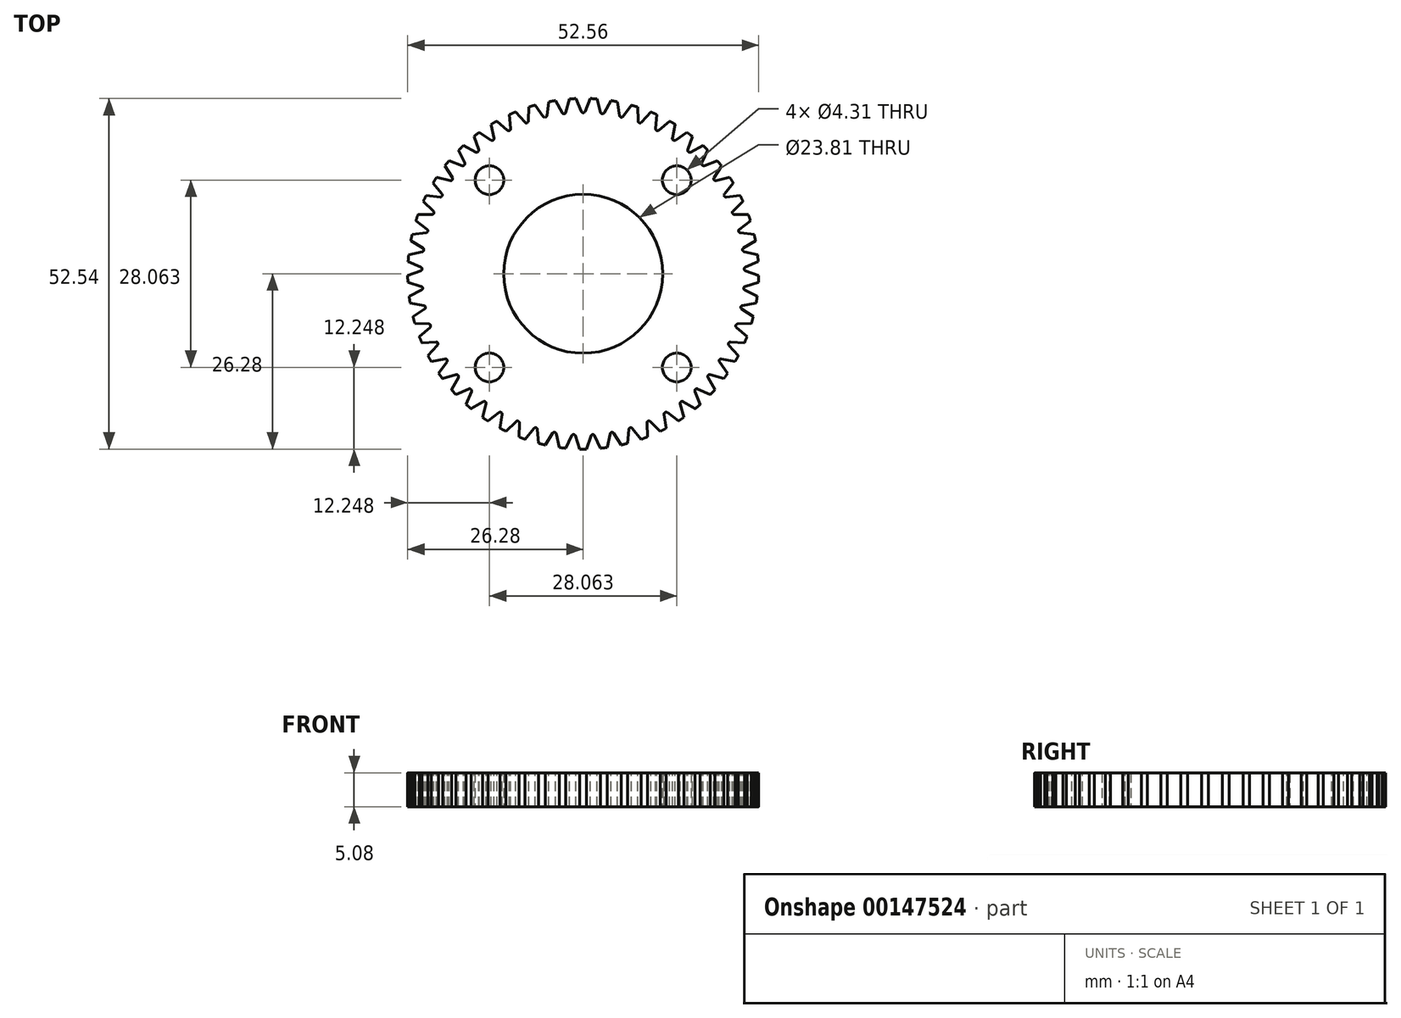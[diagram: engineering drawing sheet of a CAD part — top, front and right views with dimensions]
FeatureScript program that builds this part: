
annotation { "Feature Type Name" : "Feature", "Feature Type Description" : "" }
export const myFeature = defineFeature(function(context is Context, id is Id, definition is map)
    precondition{}
    {
        {
            var Q0;
            Q0=qCreatedBy(makeId("Top.planeOp"),FACE);
            var sketch = newSketch(context, id + "F0", { "sketchPlane" : qUnion([Q0])});
            skCircle(sketch, "E0", {"center": v(0, 0) * mm, "radius": 26.28 * mm});
            skCircle(sketch, "E1", {"center": v(0, 0) * mm, "radius": 11.9 * mm});
            skLineSegment(sketch, "E2.bottom", {"start": v(14.03, -14.03) * mm, "end": v(-14.03, -14.03) * mm, "construction": true});
            skLineSegment(sketch, "E2.top", {"start": v(14.03, 14.03) * mm, "end": v(-14.03, 14.03) * mm, "construction": true});
            skLineSegment(sketch, "E2.left", {"start": v(14.03, -14.03) * mm, "end": v(14.03, 14.03) * mm, "construction": true});
            skLineSegment(sketch, "E2.right", {"start": v(-14.03, -14.03) * mm, "end": v(-14.03, 14.03) * mm, "construction": true});
            skCircle(sketch, "E3", {"center": v(14.03, -14.03) * mm, "radius": 3.97 * mm, "construction": true});
            skCircle(sketch, "E4", {"center": v(14.03, 14.03) * mm, "radius": 2.15 * mm});
            skCircle(sketch, "E5", {"center": v(-14.03, -14.03) * mm, "radius": 2.15 * mm});
            skCircle(sketch, "E6", {"center": v(14.03, -14.03) * mm, "radius": 2.15 * mm});
            skCircle(sketch, "E7", {"center": v(-14.03, 14.03) * mm, "radius": 2.15 * mm});
            skCircle(sketch, "E8", {"center": v(0, 0) * mm, "radius": 15.88 * mm, "construction": true});
            skSolve(sketch);
        }
        {
            var Q0;
            Q0=qSketchRegion(id+"F0",true);
            extrude(context, id + "F1", {"entities" : qUnion([Q0]), "depth" : 5.08 * mm});
        }
        {
            var Q0;
            Q0=makeQuery(id+"F1.opExtrude","CAP_FACE",FACE,{"disambiguationData":[OSD([sQuery(id+"F0.wireOp",EDGE,"E0")])],"isStart":false});
            var sketch = newSketch(context, id + "F2", { "sketchPlane" : qUnion([Q0])});
            skLineSegment(sketch, "E9", {"start": v(0, 0) * mm, "end": v(0, 26.28) * mm});
            skArc(sketch, "E10", {"start": v(1.06, 26.26) * mm, "mid": v(0, 26.28) * mm, "end": v(-1.06, 26.26) * mm});
            skLineSegment(sketch, "E11", {"start": v(-1.06, 26.26) * mm, "end": v(-0.28, 24.32) * mm});
            skLineSegment(sketch, "E12", {"start": v(1.06, 26.26) * mm, "end": v(0.28, 24.32) * mm});
            skArc(sketch, "E13", {"start": v(-0.28, 24.32) * mm, "mid": v(0, 24.13) * mm, "end": v(0.28, 24.32) * mm});
            skLineSegment(sketch, "E14", {"start": v(0, 0) * mm, "end": v(0.7, 26.27) * mm, "construction": true});
            skPoint(sketch, "E15", {"position": v(0.67, 25.3) * mm});
            skSolve(sketch);
        }
        {
            var Q0;
            Q0=qSketchRegion(id+"F2",true);
            var Q1;
            Q1=makeQuery(id+"F1.opExtrude","CAP_FACE",FACE,{"disambiguationData":[OSD([sQuery(id+"F0.wireOp",EDGE,"E0")])],"isStart":true});
            extrude(context, id + "F3", {"entities" : qUnion([Q0]), "operationType" : NewBodyOperationType.REMOVE, "endBound" : BoundingType.UP_TO_SURFACE, "oppositeDirection" : true, "endBoundEntityFace" : qUnion([Q1]), "depth" : 25.4 * mm});
        }
        {
            var Q0;
            Q0=makeQuery(id+"F3.boolean.opBoolean","COPY",FACE,{"derivedFrom":makeQuery(id+"F3.opExtrude","SWEPT_FACE",FACE,{"disambiguationData":[OSD([sQuery(id+"F2.wireOp",EDGE,"E12")])]})});
            var Q1;
            Q1=makeQuery(id+"F3.boolean.opBoolean","COPY",FACE,{"derivedFrom":makeQuery(id+"F3.opExtrude","SWEPT_FACE",FACE,{"disambiguationData":[OSD([sQuery(id+"F2.wireOp",EDGE,"E13")])]})});
            var Q2;
            Q2=makeQuery(id+"F3.boolean.opBoolean","COPY",FACE,{"derivedFrom":makeQuery(id+"F3.opExtrude","SWEPT_FACE",FACE,{"disambiguationData":[OSD([sQuery(id+"F2.wireOp",EDGE,"E11")])]})});
            var Q3;
            Q3=makeQuery(id+"F1.opExtrude","SWEPT_FACE",FACE,{"disambiguationData":[OSD([sQuery(id+"F0.wireOp",EDGE,"E0")])]});
            circularPattern(context, id + "F4", {"patternType" : PatternType.FACE, "faces" : qUnion([Q0, Q1, Q2]), "axis" : qUnion([Q3]), "angle" : 6.8 * degree, "instanceCount" : 53});
        }
    });
